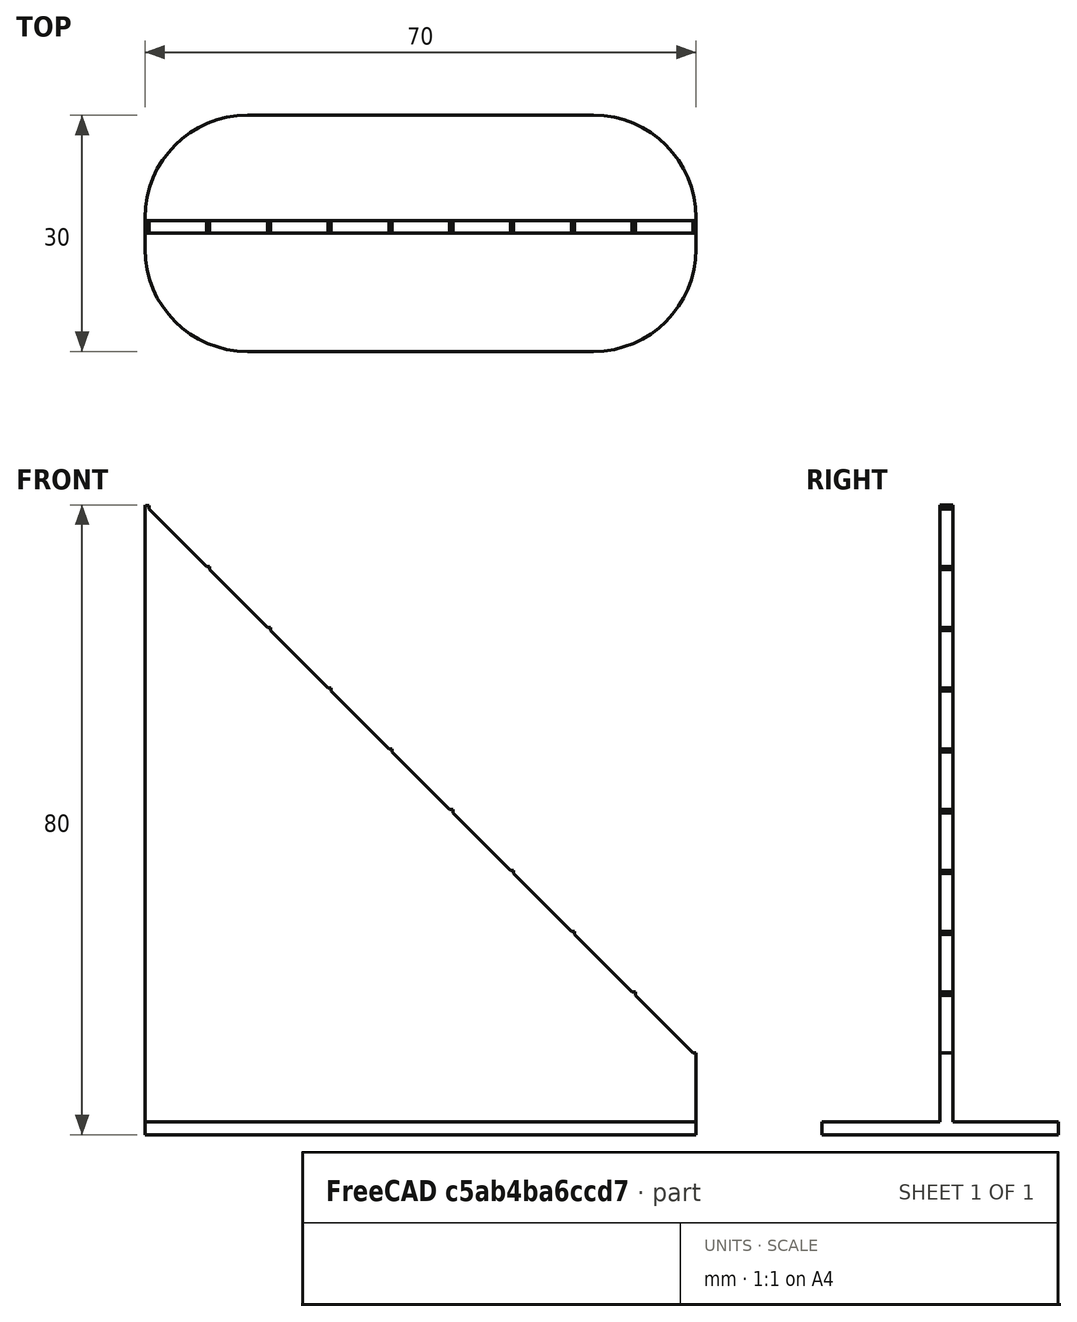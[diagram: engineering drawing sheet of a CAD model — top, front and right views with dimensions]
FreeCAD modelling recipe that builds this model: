
FCSTD DOCUMENT  (FreeCAD 1.0R39319 (Git))
Label: slantedSupport
License: All rights reserved
LicenseURL: https://en.wikipedia.org/wiki/All_rights_reserved
objects: Sketcher::SketchObject×3, PartDesign::Pad×3, App::Link×2, App::FeaturePython×2, PartDesign::Fillet×1, PartDesign::LinearPattern×1, PartDesign::Body×1, Assembly::JointGroup×1, Assembly::AssemblyObject×1
note: 21 computed .brp shape members not serialized (recipe doc carries the construction recipe); baked Part::Feature solids carry a one-line shape summary decoded from their .brp
EXTERNAL_REF file=../../print/household/to_print/repos/shelf.FCStd obj=Body002

FEATURE [Sketcher::SketchObject] Sketch
  ArcFitTolerance = 1e-06
  AttachmentSupport = -> [XZ_Plane]
  FullyConstrained = true
  MakeInternals = false
  MapMode = 5
  Placement = pos=(0,0,0) rot=(1,0,0;1.5708rad)
  sketch-geometry (6):
    g0: LineSegment StartX=0 StartY=0 StartZ=0 EndX=70 EndY=0 EndZ=0
    g1: LineSegment StartX=70 StartY=0 StartZ=0 EndX=70 EndY=10 EndZ=0
    g2: LineSegment [constr] StartX=70 StartY=10 StartZ=0 EndX=0 EndY=10 EndZ=0
    g3: LineSegment StartX=0 StartY=10 StartZ=0 EndX=0 EndY=0 EndZ=0
    g4: LineSegment StartX=0 StartY=10 StartZ=0 EndX=0 EndY=80 EndZ=0
    g5: LineSegment StartX=0 StartY=80 StartZ=0 EndX=70 EndY=10 EndZ=0
  constraints (16):
    c: Coincident(g0,g-1)
    c: PointOnObject(g0,g-1)
    c: Coincident(g1,g0)
    c: Vertical(g1)
    c: Coincident(g2,g1)
    c: Horizontal(g2)
    c: Coincident(g3,g2)
    c: Coincident(g3,g0)
    c: Vertical(g3)
    c: Coincident(g4,g2)
    c: PointOnObject(g4,g-2)
    c: Coincident(g5,g4)
    c: Coincident(g5,g1)
    c: Equal(g2,g4)
    c: Distance(g1,g1) = 10
    c: DistanceY(g4,g4) = 70
FEATURE [PartDesign::Pad] Pad
  Direction = (0,-1,2e-16)
  Length = 1.6
  Length2 = 10
  Placement = pos=(0,0,0) rot=(1,0,0;1.5708rad)
  Profile = -> Sketch
  ReferenceAxis = -> Sketch [N_Axis]
  Refine = true
  Suppressed = false
  Type = 0
FEATURE [Sketcher::SketchObject] Sketch001
  ArcFitTolerance = 1e-06
  AttachmentSupport = -> [Pad]
  ExternalGeometry = -> [Pad]
  FullyConstrained = true
  MakeInternals = false
  MapMode = 5
  Placement = pos=(0,-1.6,0) rot=(1,0,0;1.5708rad)
  sketch-geometry (4):
    g0: LineSegment StartX=0 StartY=0 StartZ=0 EndX=0 EndY=1.6 EndZ=0
    g1: LineSegment StartX=0 StartY=1.6 StartZ=0 EndX=70 EndY=1.6 EndZ=0
    g2: LineSegment StartX=70 StartY=1.6 StartZ=0 EndX=70 EndY=0 EndZ=0
    g3: LineSegment StartX=70 StartY=0 StartZ=0 EndX=0 EndY=0 EndZ=0
  constraints (10):
    c: Coincident(g0,g-1)
    c: PointOnObject(g0,g-4)
    c: Coincident(g1,g0)
    c: PointOnObject(g1,g-3)
    c: Horizontal(g1)
    c: Coincident(g2,g1)
    c: Coincident(g2,g-3)
    c: Coincident(g3,g2)
    c: Coincident(g3,g0)
    c: Distance(g0,g0) = 1.6
FEATURE [PartDesign::Pad] Pad001
  BaseFeature = -> Pad
  Direction = (0,-1,2e-16)
  Length = 30
  Length2 = 10
  Midplane = true
  Placement = pos=(0,0,0) rot=(1,0,0;1.5708rad)
  Profile = -> Sketch001
  ReferenceAxis = -> Sketch001 [N_Axis]
  Refine = true
  Suppressed = false
  Type = 0
FEATURE [PartDesign::Fillet] Fillet
  Base = -> Pad001 [Edge1,Edge20,Edge21,Edge3]
  BaseFeature = -> Pad001
  Placement = pos=(0,0,0) rot=(1,0,0;1.5708rad)
  Radius = 13
  Refine = true
  SupportTransform = false
  Suppressed = false
  UseAllEdges = false
FEATURE [Sketcher::SketchObject] Sketch002
  ArcFitTolerance = 1e-06
  AttachmentSupport = -> [Fillet]
  ExternalGeometry = -> [Fillet]
  FullyConstrained = true
  MakeInternals = false
  MapMode = 5
  Placement = pos=(0,-1.6,0) rot=(1,0,0;1.5708rad)
  sketch-geometry (3):
    g0: LineSegment StartX=70 StartY=10 StartZ=0 EndX=70 EndY=10.4 EndZ=0
    g1: LineSegment StartX=70 StartY=10.4 StartZ=0 EndX=69.6 EndY=10.4 EndZ=0
    g2: LineSegment StartX=69.6 StartY=10.4 StartZ=0 EndX=70 EndY=10 EndZ=0
  constraints (8):
    c: Coincident(g0,g-4)
    c: Vertical(g0)
    c: Coincident(g1,g0)
    c: PointOnObject(g1,g-3)
    c: Horizontal(g1)
    c: Coincident(g2,g1)
    c: Coincident(g2,g0)
    c: Distance(g0,g0) = 0.4
FEATURE [PartDesign::Pad] Pad002
  BaseFeature = -> Fillet
  Direction = (0,-1,2e-16)
  Length = 10
  Length2 = 10
  Placement = pos=(0,0,0) rot=(1,0,0;1.5708rad)
  Profile = -> Sketch002
  ReferenceAxis = -> Sketch002 [N_Axis]
  Refine = true
  Reversed = true
  Suppressed = false
  Type = 3
  UpToFace = -> Fillet [Face8]
FEATURE [PartDesign::LinearPattern] LinearPattern
  BaseFeature = -> Pad002
  Direction = -> Pad002 [Edge34]
  Length = 98.2878
  Mode = 0
  Occurrences = 10
  Offset = 10.9209
  Originals = -> [Pad002]
  Placement = pos=(0,0,0) rot=(1,0,0;1.5708rad)
  Refine = true
  Reversed = true
  Suppressed = false
  TransformMode = 0
  expr: Length = 69.5 mm * sqrt(2)
FEATURE [PartDesign::Body] Body
  AllowCompound = false
  Group = -> [Sketch,Pad,Sketch001,Pad001,Fillet,Sketch002,Pad002,LinearPattern]
  Origin = -> Origin
  Tip = -> LinearPattern
FEATURE [App::Link] Body001
  LinkedObject = -> Body
FEATURE [App::FeaturePython] GroundedJoint  # Assembly grounded joint (typed FeaturePython)
  ObjectToGround = -> Body001
FEATURE [App::Link] fridge_crate
  LinkPlacement = pos=(-301.661,-335.357,194.515) rot=(0,1,0;0.785398rad)
  LinkedObject = -> <external ../../print/household/to_print/repos/shelf.FCStd>#Body002
  Placement = pos=(-301.661,-335.357,194.515) rot=(0,1,0;0.785398rad)
FEATURE [App::FeaturePython] Joint  label="Parallel"  # Assembly joint (typed FeaturePython)
  Activated = true
  AngleMax = 0
  AngleMin = 0
  Detach1 = false
  Detach2 = false
  Distance = 0
  Distance2 = 0
  EnableAngleMax = false
  EnableAngleMin = false
  EnableLengthMax = false
  EnableLengthMin = false
  JointType = 6 (Parallel)
  LengthMax = 0
  LengthMin = 0
  Placement1 = pos=(4.16111,-0.8,75.8389) rot=(0,1,0;0.785398rad)
  Placement2 = pos=(190,45,-1.6) rot=(0,0,1;0rad)
  Reference1 = -> Assembly [Body001.LinearPattern.Face17,Body001.LinearPattern.Face17]
  Reference2 = -> Assembly [fridge_crate.Chamfer001.Face35,fridge_crate.Chamfer001.Face35]
FEATURE [Assembly::JointGroup] Joints
  Group = -> [GroundedJoint,Joint]
FEATURE [Assembly::AssemblyObject] Assembly
  Group = -> [Joints,Body001,GroundedJoint,fridge_crate,Joint]
  Origin = -> Origin001
  Type = Assembly
